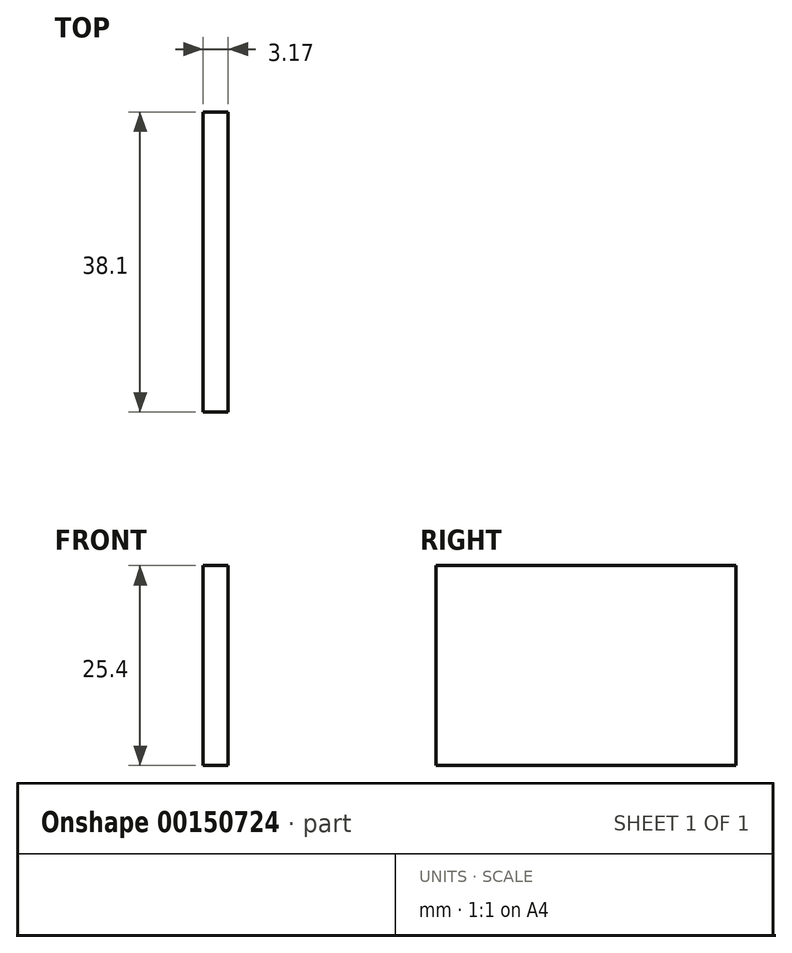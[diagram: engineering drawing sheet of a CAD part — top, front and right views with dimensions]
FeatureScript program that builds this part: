
annotation { "Feature Type Name" : "Feature", "Feature Type Description" : "" }
export const myFeature = defineFeature(function(context is Context, id is Id, definition is map)
    precondition{}
    {
        {
            var Q0;
            Q0=qCreatedBy(makeId("Right.planeOp"),FACE);
            var sketch = newSketch(context, id + "F0", { "sketchPlane" : qUnion([Q0])});
            skLineSegment(sketch, "E0.bottom", {"start": v(19.05, 12.7) * mm, "end": v(-19.05, 12.7) * mm});
            skLineSegment(sketch, "E0.top", {"start": v(19.05, -12.7) * mm, "end": v(-19.05, -12.7) * mm});
            skLineSegment(sketch, "E0.left", {"start": v(19.05, 12.7) * mm, "end": v(19.05, -12.7) * mm});
            skLineSegment(sketch, "E0.right", {"start": v(-19.05, 12.7) * mm, "end": v(-19.05, -12.7) * mm});
            skPoint(sketch, "E0.middle", {"position": v(0, 0) * mm});
            skSolve(sketch);
        }
        {
            var Q0;
            Q0 = qSketchRegion(id + "F0", true);
            extrude(context, id + "F1", {"entities" : qUnion([Q0]), "depth" : 3.17 * mm});
        }
    });
